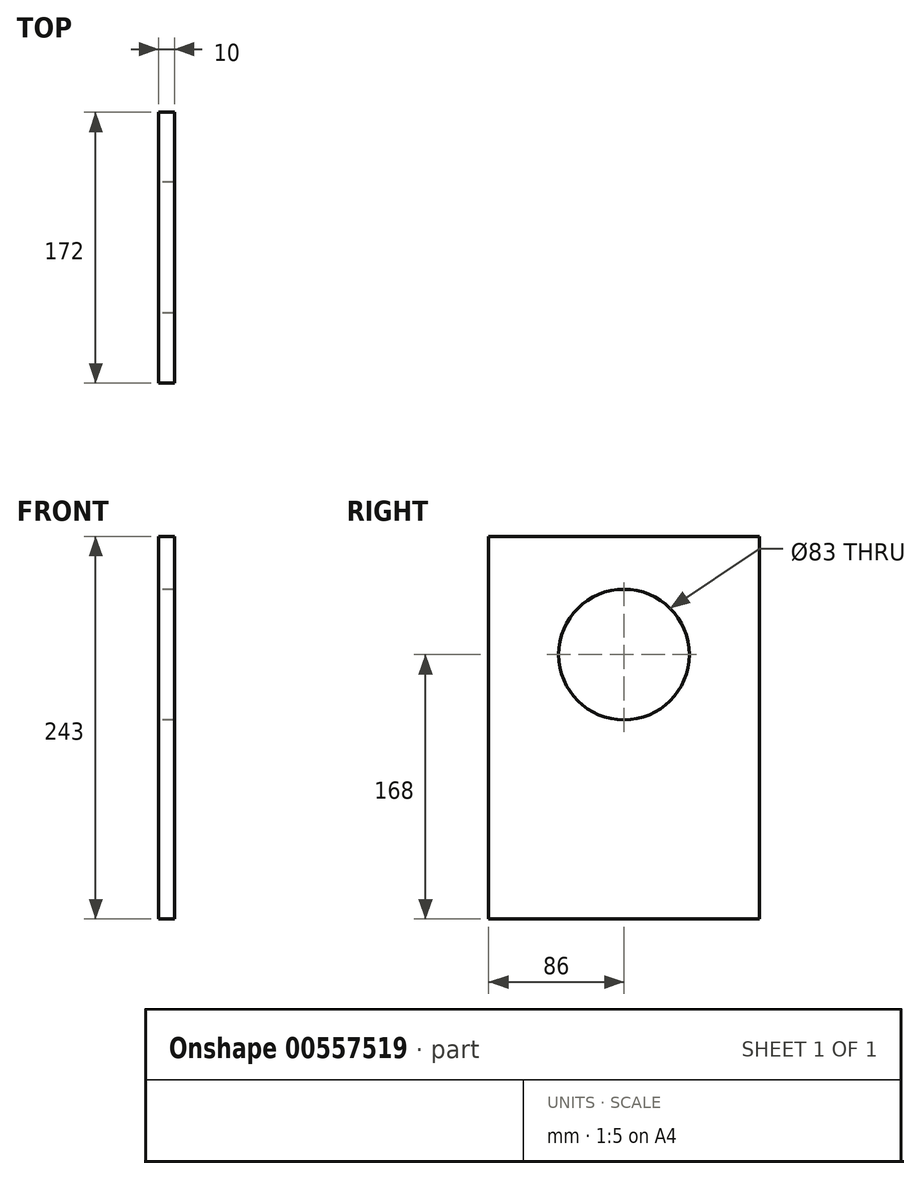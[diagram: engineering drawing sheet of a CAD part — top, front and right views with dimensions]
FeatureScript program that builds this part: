
annotation { "Feature Type Name" : "Feature", "Feature Type Description" : "" }
export const myFeature = defineFeature(function(context is Context, id is Id, definition is map)
    precondition{}
    {
        {
            var Q0;
            Q0=qCreatedBy(makeId("Right.planeOp"),FACE);
            var sketch = newSketch(context, id + "F0", { "sketchPlane" : qUnion([Q0])});
            skLineSegment(sketch, "E0.bottom", {"start": v(86, 121.5) * mm, "end": v(-86, 121.5) * mm});
            skLineSegment(sketch, "E0.top", {"start": v(86, -121.5) * mm, "end": v(-86, -121.5) * mm});
            skLineSegment(sketch, "E0.left", {"start": v(86, 121.5) * mm, "end": v(86, -121.5) * mm});
            skLineSegment(sketch, "E0.right", {"start": v(-86, 121.5) * mm, "end": v(-86, -121.5) * mm});
            skPoint(sketch, "E0.middle", {"position": v(0, 0) * mm});
            skLineSegment(sketch, "E1", {"start": v(0, 121.5) * mm, "end": v(0, 46.5) * mm});
            skPoint(sketch, "E1.endSnap0", {"position": v(0, 121.5) * mm});
            skCircle(sketch, "E2", {"center": v(0, 46.5) * mm, "radius": 41.5 * mm});
            skSolve(sketch);
        }
        {
            var Q0;
            Q0=makeQuery(id+"F0.imprint","IMPRINT",FACE,{"disambiguationData":[TD([[makeQuery(id+"F0.imprint","IMPRINT",EDGE,{"derivedFrom":sQuery(id+"F0.wireOp",EDGE,"E0.top")}),-1.0]])]});
            extrude(context, id + "F1", {"entities" : qUnion([Q0]), "depth" : 10 * mm, "offsetDistance" : 25 * mm});
        }
    });
